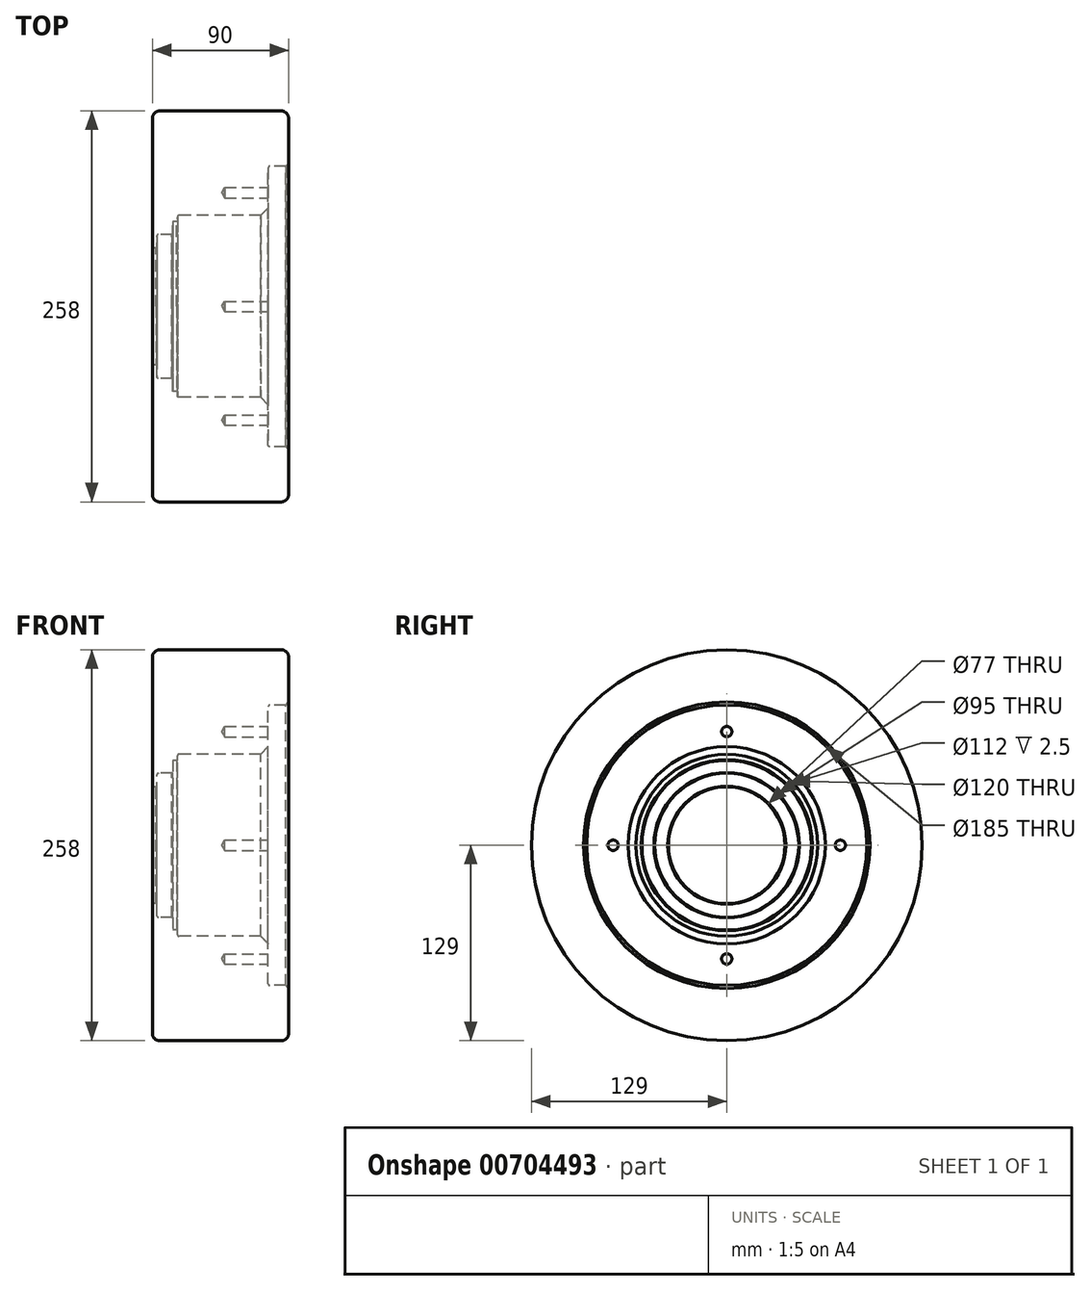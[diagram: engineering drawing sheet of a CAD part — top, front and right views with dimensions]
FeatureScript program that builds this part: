
annotation { "Feature Type Name" : "Feature", "Feature Type Description" : "" }
export const myFeature = defineFeature(function(context is Context, id is Id, definition is map)
    precondition{}
    {
        {
            var Q0;
            Q0=qCreatedBy(makeId("Front.planeOp"),FACE);
            var sketch = newSketch(context, id + "F0", { "sketchPlane" : qUnion([Q0])});
            skLineSegment(sketch, "E0", {"start": v(0, 129) * mm, "end": v(90, 129) * mm});
            skLineSegment(sketch, "E1", {"start": v(90, 129) * mm, "end": v(90, 92.5) * mm});
            skLineSegment(sketch, "E2", {"start": v(90, 92.5) * mm, "end": v(76.5, 92.5) * mm});
            skLineSegment(sketch, "E3", {"start": v(76.5, 92.5) * mm, "end": v(76.5, 60) * mm});
            skLineSegment(sketch, "E4", {"start": v(76.5, 60) * mm, "end": v(16.5, 60) * mm});
            skLineSegment(sketch, "E5", {"start": v(0, 38.5) * mm, "end": v(0, 129) * mm});
            skLineSegment(sketch, "E6", {"start": v(0, 0) * mm, "end": v(84.03, 0) * mm});
            skLineSegment(sketch, "E7", {"start": v(16.5, 60) * mm, "end": v(16.5, 56) * mm});
            skLineSegment(sketch, "E8", {"start": v(16.5, 56) * mm, "end": v(13.5, 56) * mm});
            skLineSegment(sketch, "E9", {"start": v(13.5, 56) * mm, "end": v(13.5, 47.5) * mm});
            skLineSegment(sketch, "E10", {"start": v(13.5, 47.5) * mm, "end": v(3, 47.5) * mm});
            skLineSegment(sketch, "E11", {"start": v(3, 47.5) * mm, "end": v(3, 38.5) * mm});
            skLineSegment(sketch, "E12", {"start": v(3, 38.5) * mm, "end": v(0, 38.5) * mm});
            skSolve(sketch);
        }
        {
            var Q0;
            Q0=makeQuery(id+"F0.imprint","IMPRINT",FACE,{"disambiguationData":[TD([[makeQuery(id+"F0.imprint","IMPRINT",EDGE,{"derivedFrom":sQuery(id+"F0.wireOp",EDGE,"E0")}),-1.0]])]});
            var Q1;
            Q1=sQuery(id+"F0.wireOp",EDGE,"E6");
            revolve(context, id + "F1", {"surfaceOperationType" : NewSurfaceOperationType.NEW, "entities" : qUnion([Q0]), "axis" : qUnion([Q1]), "revolveType" : RevolveType.FULL});
        }
        {
            var Q0;
            Q0=makeQuery(id+"F1.opRevolve","SWEPT_EDGE",EDGE,{"disambiguationData":[OSD([sQuery(id+"F0.wireOp",EDGE,"E0"),sQuery(id+"F0.wireOp",EDGE,"E1")])]});
            var Q1;
            Q1=makeQuery(id+"F1.opRevolve","SWEPT_EDGE",EDGE,{"disambiguationData":[OSD([sQuery(id+"F0.wireOp",EDGE,"E0"),sQuery(id+"F0.wireOp",EDGE,"E5")])]});
            fillet(context, id + "F2", {"entities" : qUnion([Q0, Q1]), "radius" : 5 * mm, "tangentPropagation" : true, "allowEdgeOverflow" : false});
        }
        {
            var Q0;
            Q0=makeQuery(id+"F1.opRevolve","SWEPT_EDGE",EDGE,{"disambiguationData":[OSD([sQuery(id+"F0.wireOp",EDGE,"E5"),sQuery(id+"F0.wireOp",EDGE,"E12")])]});
            var Q1;
            Q1=makeQuery(id+"F1.opRevolve","SWEPT_EDGE",EDGE,{"disambiguationData":[OSD([sQuery(id+"F0.wireOp",EDGE,"E11"),sQuery(id+"F0.wireOp",EDGE,"E12")])]});
            var Q2;
            Q2=makeQuery(id+"F1.opRevolve","SWEPT_EDGE",EDGE,{"disambiguationData":[OSD([sQuery(id+"F0.wireOp",EDGE,"E9"),sQuery(id+"F0.wireOp",EDGE,"E10")])]});
            var Q3;
            Q3=makeQuery(id+"F1.opRevolve","SWEPT_EDGE",EDGE,{"disambiguationData":[OSD([sQuery(id+"F0.wireOp",EDGE,"E7"),sQuery(id+"F0.wireOp",EDGE,"E8")])]});
            chamfer(context, id + "F3", {"entities" : qUnion([Q0, Q1, Q2, Q3]), "width" : 0.5 * mm, "tangentPropagation" : true});
        }
        {
            var Q0;
            Q0=makeQuery(id+"F1.opRevolve","SWEPT_EDGE",EDGE,{"disambiguationData":[OSD([sQuery(id+"F0.wireOp",EDGE,"E3"),sQuery(id+"F0.wireOp",EDGE,"E4")])]});
            chamfer(context, id + "F4", {"entities" : qUnion([Q0]), "width" : 5 * mm, "tangentPropagation" : true});
        }
        {
            var Q0;
            Q0=makeQuery(id+"F1.opRevolve","SWEPT_EDGE",EDGE,{"disambiguationData":[OSD([sQuery(id+"F0.wireOp",EDGE,"E1"),sQuery(id+"F0.wireOp",EDGE,"E2")])]});
            chamfer(context, id + "F5", {"entities" : qUnion([Q0]), "width" : 2 * mm, "tangentPropagation" : true});
        }
        {
            var Q0;
            Q0=makeQuery(id+"F1.opRevolve","SWEPT_EDGE",EDGE,{"disambiguationData":[OSD([sQuery(id+"F0.wireOp",EDGE,"E2"),sQuery(id+"F0.wireOp",EDGE,"E3")])]});
            var Q1;
            Q1=makeQuery(id+"F1.opRevolve","SWEPT_EDGE",EDGE,{"disambiguationData":[OSD([sQuery(id+"F0.wireOp",EDGE,"E4"),sQuery(id+"F0.wireOp",EDGE,"E7")])]});
            var Q2;
            Q2=makeQuery(id+"F1.opRevolve","SWEPT_EDGE",EDGE,{"disambiguationData":[OSD([sQuery(id+"F0.wireOp",EDGE,"E10"),sQuery(id+"F0.wireOp",EDGE,"E11")])]});
            fillet(context, id + "F6", {"entities" : qUnion([Q0, Q1, Q2]), "radius" : 1 * mm, "tangentPropagation" : true, "allowEdgeOverflow" : false});
        }
        {
            var Q0;
            Q0=makeQuery(id+"F1.opRevolve","SWEPT_FACE",FACE,{"disambiguationData":[OSD([sQuery(id+"F0.wireOp",EDGE,"E3")])]});
            var sketch = newSketch(context, id + "F7", { "sketchPlane" : qUnion([Q0])});
            skPoint(sketch, "E13", {"position": v(0, 75) * mm});
            skPoint(sketch, "E14", {"position": v(-75, 0) * mm});
            skPoint(sketch, "E15", {"position": v(0, -75) * mm});
            skPoint(sketch, "E16", {"position": v(75, 0) * mm});
            skCircle(sketch, "E17", {"center": v(0, 0) * mm, "radius": 75 * mm});
            skSolve(sketch);
        }
        {
            var Q0;
            Q0=sQuery(id+"F7.wireOp",VERTEX,"E13");
            var Q1;
            Q1=sQuery(id+"F7.wireOp",VERTEX,"E14");
            var Q2;
            Q2=sQuery(id+"F7.wireOp",VERTEX,"E15");
            var Q3;
            Q3=sQuery(id+"F7.wireOp",VERTEX,"E16");
            var Q4;
            Q4=makeQuery(id+"F1.opRevolve","SWEPT_BODY",BODY,{"disambiguationData":[OSD([sQuery(id+"F0.wireOp",EDGE,"E0"),sQuery(id+"F0.wireOp",EDGE,"E1"),sQuery(id+"F0.wireOp",EDGE,"E2"),sQuery(id+"F0.wireOp",EDGE,"E3"),sQuery(id+"F0.wireOp",EDGE,"E4"),sQuery(id+"F0.wireOp",EDGE,"E5"),sQuery(id+"F0.wireOp",EDGE,"E7"),sQuery(id+"F0.wireOp",EDGE,"E8"),sQuery(id+"F0.wireOp",EDGE,"E9"),sQuery(id+"F0.wireOp",EDGE,"E10"),sQuery(id+"F0.wireOp",EDGE,"E11"),sQuery(id+"F0.wireOp",EDGE,"E12")])]});
            hole(context, id + "F8", {"style" : HoleStyle.SIMPLE, "endStyle" : HoleEndStyle.BLIND, "standardTappedOrClearance" : lookupTablePath({ "standard" : "ISO", "engagement" : "75%", "pitch" : "1.25 mm", "size" : "M8", "type" : "Tapped" }), "standardBlindInLast" : lookupTablePath({ "standard" : "ISO", "engagement" : "75%", "pitch" : "1.25 mm", "size" : "M8", "type" : "Tapped" }), "holeDiameter" : 6.8 * mm, "majorDiameter" : 8 * mm, "showTappedDepth" : true, "holeDepth" : 28.75 * mm, "isTappedThrough" : true, "tappedDepth" : 25 * mm, "tapClearance" : 3, "startFromSketch" : true, "locations" : qUnion([Q0, Q1, Q2, Q3]), "scope" : qUnion([Q4])});
        }
    });
